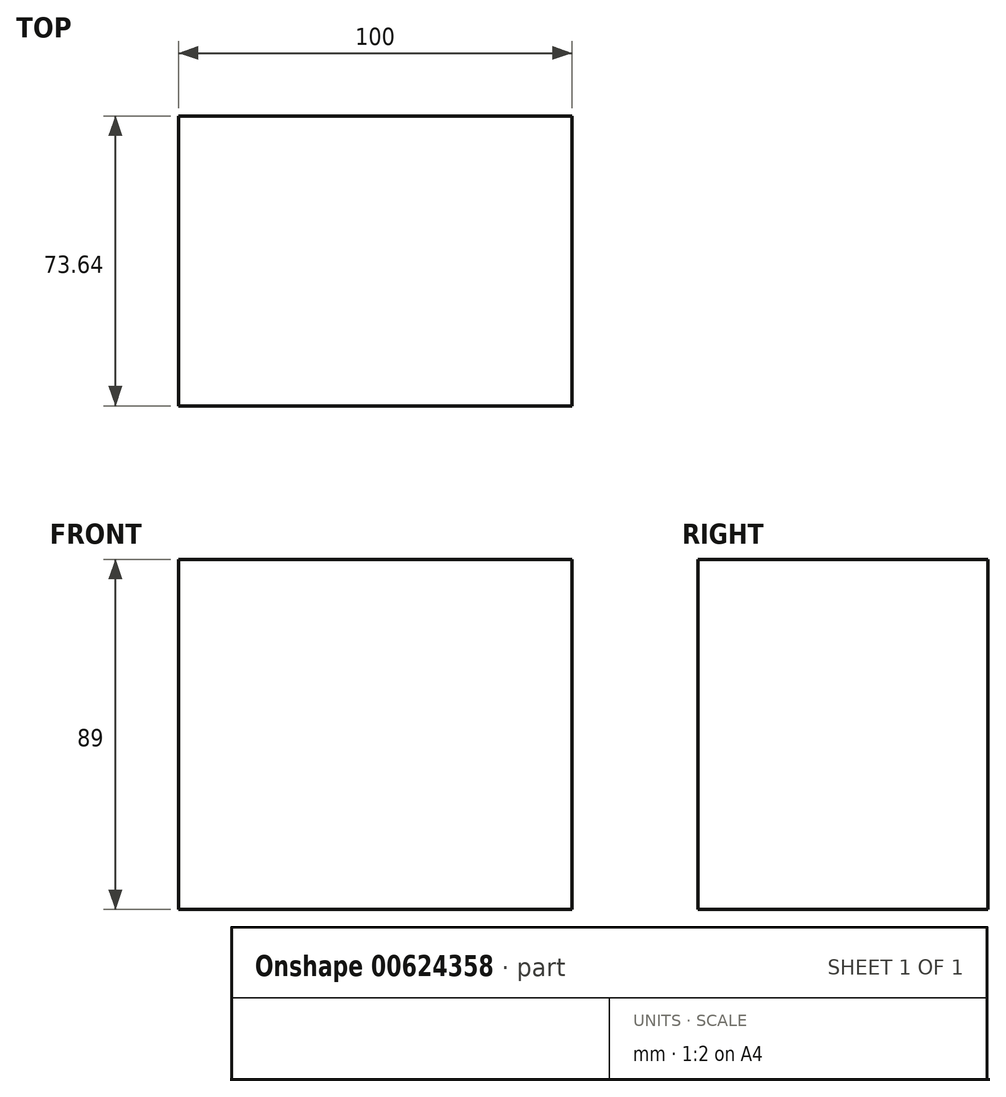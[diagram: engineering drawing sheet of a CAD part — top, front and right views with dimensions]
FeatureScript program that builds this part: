
annotation { "Feature Type Name" : "Feature", "Feature Type Description" : "" }
export const myFeature = defineFeature(function(context is Context, id is Id, definition is map)
    precondition{}
    {
        {
            var Q0;
            Q0=qCreatedBy(makeId("Top.planeOp"),FACE);
            var sketch = newSketch(context, id + "F0", { "sketchPlane" : qUnion([Q0])});
            skLineSegment(sketch, "E0.bottom", {"start": v(50, -36.82) * mm, "end": v(-50, -36.82) * mm});
            skLineSegment(sketch, "E0.top", {"start": v(50, 36.82) * mm, "end": v(-50, 36.82) * mm});
            skLineSegment(sketch, "E0.left", {"start": v(50, -36.82) * mm, "end": v(50, 36.82) * mm});
            skLineSegment(sketch, "E0.right", {"start": v(-50, -36.82) * mm, "end": v(-50, 36.82) * mm});
            skPoint(sketch, "E0.middle", {"position": v(0, 0) * mm});
            skSolve(sketch);
        }
        {
            var Q0;
            Q0=makeQuery(id+"F0.imprint","IMPRINT",FACE,{"disambiguationData":[TD([[makeQuery(id+"F0.imprint","IMPRINT",EDGE,{"derivedFrom":sQuery(id+"F0.wireOp",EDGE,"E0.bottom")}),-1.0]])]});
            extrude(context, id + "F1", {"entities" : qUnion([Q0]), "depth" : 89 * mm, "offsetDistance" : 25 * mm});
        }
        {
            var Q0;
            Q0=qCreatedBy(makeId("Front.planeOp"),FACE);
            var sketch = newSketch(context, id + "F2", { "sketchPlane" : qUnion([Q0])});
            skLineSegment(sketch, "E1.0", {"start": v(50, 89) * mm, "end": v(-50, 89) * mm});
            skArc(sketch, "E2", {"start": v(0, 71.9) * mm, "mid": v(17.1, 89) * mm, "end": v(0, 106.1) * mm});
            skLineSegment(sketch, "E3", {"start": v(0, 106.1) * mm, "end": v(0, 71.9) * mm});
            skSolve(sketch);
        }
        {
            var Q0;
            Q0=sQuery(id+"F2.wireOp",EDGE,"E2");
            var Q1;
            Q1=sQuery(id+"F2.wireOp",EDGE,"E3");
            revolve(context, id + "F3", {"bodyType" : ToolBodyType.SURFACE, "surfaceEntities" : qUnion([Q0]), "axis" : qUnion([Q1]), "revolveType" : RevolveType.FULL});
        }
    });
